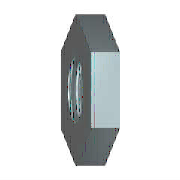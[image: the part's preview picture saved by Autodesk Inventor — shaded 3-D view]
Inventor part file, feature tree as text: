
AUTODESK INVENTOR PART (.ipt)
format: ipt  version: 2017 (Build 210142000, 142)  size: 126,464 bytes
history: native  units: mm (DEFAULTED — no unit token found)
features: other x4, sketch x2, extrude x1, chamfer x1
ambient origin geometry x8: Origin, YZ Plane, XZ Plane, XY Plane, X Axis, Y Axis, Z Axis, Center Point
bodies: Solid1 (feature_tree)
feature tree (8):
  extrude  "Extrusion1"  TaperAngle=0.0deg  [1 undecoded]
  other  "MSC_A1"
  other  "MSC_PT1"
  other  "MSC_PT2"
  other  "MSC_PF1"
  chamfer  "Chamfer1"  [1 undecoded]
  sketch  "Sketch1"  dims[d2=0.0mm]
  sketch  "Sketch2"  dims[d3=4.134mm d4=2.7mm d5=4.0mm d6=2.0mm d7=60.0deg d8=8.0mm d9=20.594885mm d14=0.0mm d15=0.0mm d16=0.0mm d17=0.48mm d18=0.48mm d20=45.0deg d21=0.0mm d23=0.0mm d24=0.0mm d25=0.0mm]
note: 2 required parameter values undecoded (feature->parameter linkage not recoverable at this tier; creation-order binding heuristic only, values carry confidence <= 0.55)
